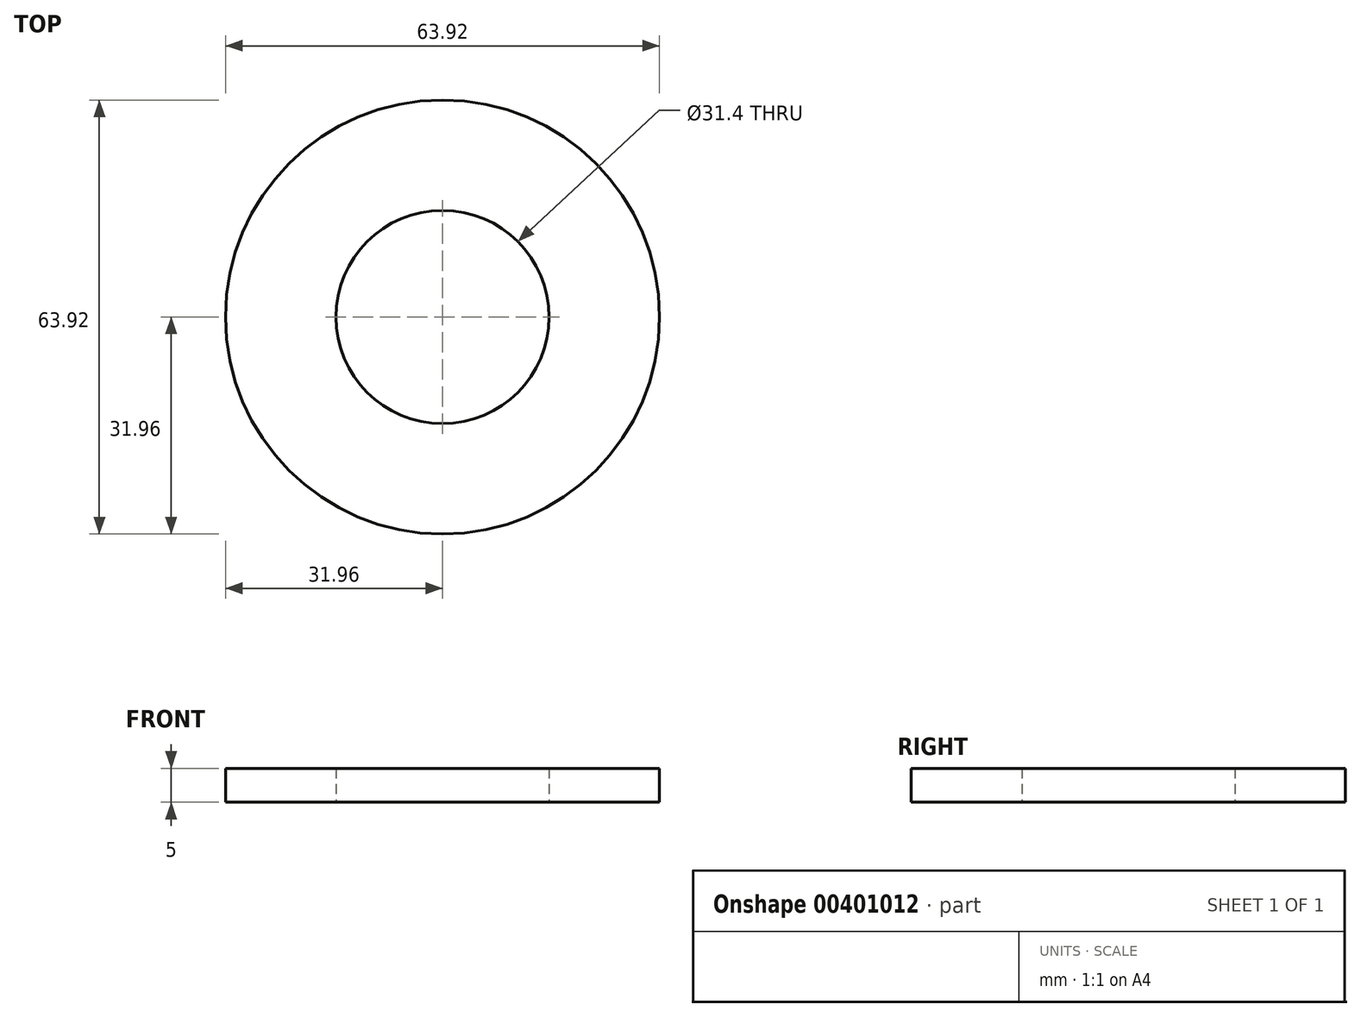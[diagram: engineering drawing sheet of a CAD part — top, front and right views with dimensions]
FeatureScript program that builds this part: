
annotation { "Feature Type Name" : "Feature", "Feature Type Description" : "" }
export const myFeature = defineFeature(function(context is Context, id is Id, definition is map)
    precondition{}
    {
        {
            var Q0;
            Q0=qCreatedBy(makeId("Top.planeOp"),FACE);
            var sketch = newSketch(context, id + "F0", { "sketchPlane" : qUnion([Q0])});
            skCircle(sketch, "E0", {"center": v(0, 0) * mm, "radius": 15.7 * mm});
            skCircle(sketch, "E1", {"center": v(0, 0) * mm, "radius": 31.96 * mm});
            skSolve(sketch);
        }
        {
            var Q0;
            Q0 = qSketchRegion(id + "F0", true);
            extrude(context, id + "F1", {"entities" : qUnion([Q0]), "depth" : 5 * mm});
        }
    });
